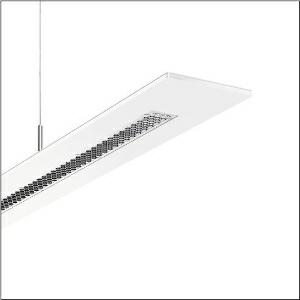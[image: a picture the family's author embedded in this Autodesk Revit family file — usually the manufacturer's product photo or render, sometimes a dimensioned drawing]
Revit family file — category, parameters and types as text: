
# Revit family: arktika_r__21_5mb2512l30830_74ae
name_source: partatom
category: Lighting Fixtures
units: mm (PartAtom-declared; Revit-internal decimal feet)

## family parameters
Cut with Voids When Loaded = No
Host = Face
Light Source = No
Part Type = Normal
Room Calculation Point = No
Round Connector Dimension = Use Diameter
Shared = No

## types (1)
- Arktika® 21 (1 x LED 3000K / CRI = 80 (unbekannt), 3670 lm, 3000K)
    Apparent Load = 31 VA
    CIE Flux Codes = 81 100 100 79 100
    Color Rendering = 80
    Color Temperature = 3000K
    Default Elevation = 1800 mm
    Description = Arktika® 21, office luminaire, primary anti-glare with honeycomb louvre, of plastic, aluminium vaporised, highly specular, light emission: direct/indirect distribution, primary light characteristic: symmetric, installation type: suspended mounting, LED, rated luminous flux: 3.670lm, luminous efficacy: 120lm/W, light colour: 830, colour temperature: 3000K, control gear: ON/OFF, with terminal, 3-pole, mains connection: 220..240V, AC, 50/60Hz, rated input power: 31W, housing, of aluminium, powder-coated, traffic white (RAL 9016), 1-length, length: 1.250mm, width: 120mm, height: 8mm, protection rating (complete): IP20, insulation class (complete): insulation class II (safety insulation), certification: CE, packaging unit: 1 piece
    Height = 8 mm  [stored 0.0262467 ft]
    Lamp = 1 x LED 3000K / CRI >= 80 (unbekannt)
    Lamp Light Flux = 3670 lm
    Lamp count = 1
    Length = 1250 mm
    Luminous efficacy = 120 lm/W
    Manufacturer = Siteco
    ModVariant = No
    Model = 5MB2512L30830
    Mounting Place = Ceiling
    Mounting Type = Pendant
    Number of Poles = 1
    OnlyDefault = Yes
    Power Factor = 1
    Product Name = Arktika® 21
    Product group = office luminaire | ceiling pendant
    ProductGroupID = 904
    Protection Class = Protection class II
    Protection Degree = IP 20
    RLX_Detail_Level = 1
    RLX_Emergency_Light_Flux = 0 lm
    RLX_Emergency_Type = 0
    RLX_Emergency_Type_DB = No
    RlxData = <blob elided: 36029 chars, md5=4e0864a3>
    Socket = socket
    Standby Power = 0 W
    System Light Flux = 3670 lm
    System Power = 31 W
    Type Comments = Product without accessories
    Type Image = l_1006128.jpg
    URL = http://relux.com
    VarID = ---
    Voltage = 0 V
    Weight = 0.00 kg
    Width = 120 mm

note: [stored X ft] marks values corroborated as IEEE doubles in the binary element streams (Revit-internal decimal feet)

## geometry (parser evidence)
native form markers: Blend x4, Sweep x12
no freeform markers — native parametric forms only
